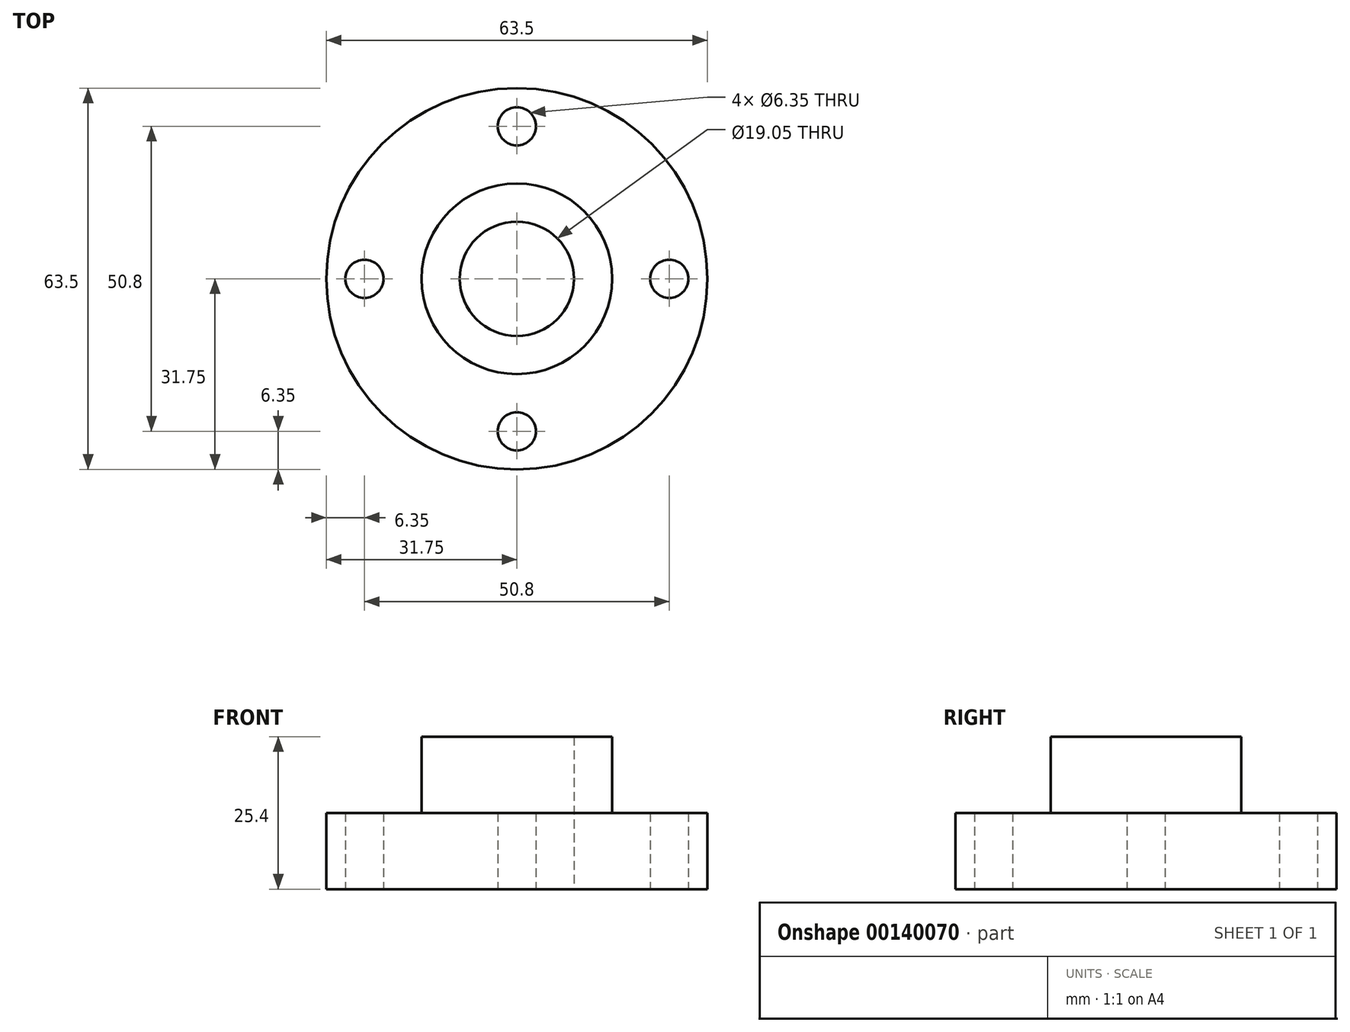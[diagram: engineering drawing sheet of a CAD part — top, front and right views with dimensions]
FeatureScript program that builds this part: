
annotation { "Feature Type Name" : "Feature", "Feature Type Description" : "" }
export const myFeature = defineFeature(function(context is Context, id is Id, definition is map)
    precondition{}
    {
        {
            var Q0;
            Q0=qCreatedBy(makeId("Top.planeOp"),FACE);
            var sketch = newSketch(context, id + "F0", { "sketchPlane" : qUnion([Q0])});
            skCircle(sketch, "E0", {"center": v(0, 0) * mm, "radius": 31.75 * mm});
            skCircle(sketch, "E1", {"center": v(0, 0) * mm, "radius": 25.4 * mm, "construction": true});
            skSolve(sketch);
        }
        {
            var Q0;
            Q0=makeQuery(id+"F0.imprint","IMPRINT",FACE,{"disambiguationData":[TD([[makeQuery(id+"F0.imprint","IMPRINT",EDGE,{"derivedFrom":sQuery(id+"F0.wireOp",EDGE,"E0")}),1.0]])]});
            extrude(context, id + "F1", {"entities" : qUnion([Q0]), "depth" : 12.7 * mm});
        }
        {
            var Q0;
            Q0=qCreatedBy(makeId("Top.planeOp"),FACE);
            var sketch = newSketch(context, id + "F2", { "sketchPlane" : qUnion([Q0])});
            skCircle(sketch, "E2", {"center": v(0, 0) * mm, "radius": 15.88 * mm});
            skCircle(sketch, "E3", {"center": v(0, 0) * mm, "radius": 9.53 * mm});
            skSolve(sketch);
        }
        {
            var Q0;
            Q0 = qSketchRegion(id + "F2", true);
            extrude(context, id + "F3", {"entities" : qUnion([Q0]), "operationType" : NewBodyOperationType.ADD, "depth" : 25.4 * mm});
        }
        {
            var Q0;
            Q0=makeQuery(id+"F3.boolean.opBoolean","SPLIT",FACE,{"disambiguationData":[TD([makeQuery(id+"F3.opExtrude","SWEPT_FACE",FACE,{"disambiguationData":[OSD([sQuery(id+"F2.wireOp",EDGE,"E3")])]})])],"derivedFrom":makeQuery(id+"F1.opExtrude","CAP_FACE",FACE,{"disambiguationData":[OSD([sQuery(id+"F0.wireOp",EDGE,"E0")])],"isStart":false})});
            extrude(context, id + "F4", {"entities" : qUnion([Q0]), "operationType" : NewBodyOperationType.REMOVE, "endBound" : BoundingType.THROUGH_ALL, "oppositeDirection" : true, "depth" : 25.4 * mm});
        }
        {
            var Q0;
            Q0=qCreatedBy(makeId("Top.planeOp"),FACE);
            var sketch = newSketch(context, id + "F5", { "sketchPlane" : qUnion([Q0])});
            skPoint(sketch, "E4.center", {"position": v(0, 0.47) * mm});
            skPoint(sketch, "E5.center", {"position": v(0, 0) * mm});
            skLineSegment(sketch, "E6", {"start": v(0, 41.54) * mm, "end": v(0, -42.18) * mm, "construction": true});
            skLineSegment(sketch, "E7", {"start": v(-46.17, 0) * mm, "end": v(54.14, 0) * mm, "construction": true});
            skCircle(sketch, "E8", {"center": v(0, 25.4) * mm, "radius": 3.18 * mm});
            skCircle(sketch, "E9", {"center": v(25.4, 0) * mm, "radius": 3.18 * mm});
            skCircle(sketch, "E10", {"center": v(0, -25.4) * mm, "radius": 3.18 * mm});
            skCircle(sketch, "E11", {"center": v(-25.4, 0) * mm, "radius": 3.18 * mm});
            skSolve(sketch);
        }
        {
            var Q0;
            Q0 = qSketchRegion(id + "F5", true);
            extrude(context, id + "F6", {"entities" : qUnion([Q0]), "operationType" : NewBodyOperationType.REMOVE, "depth" : 25.4 * mm});
        }
    });
